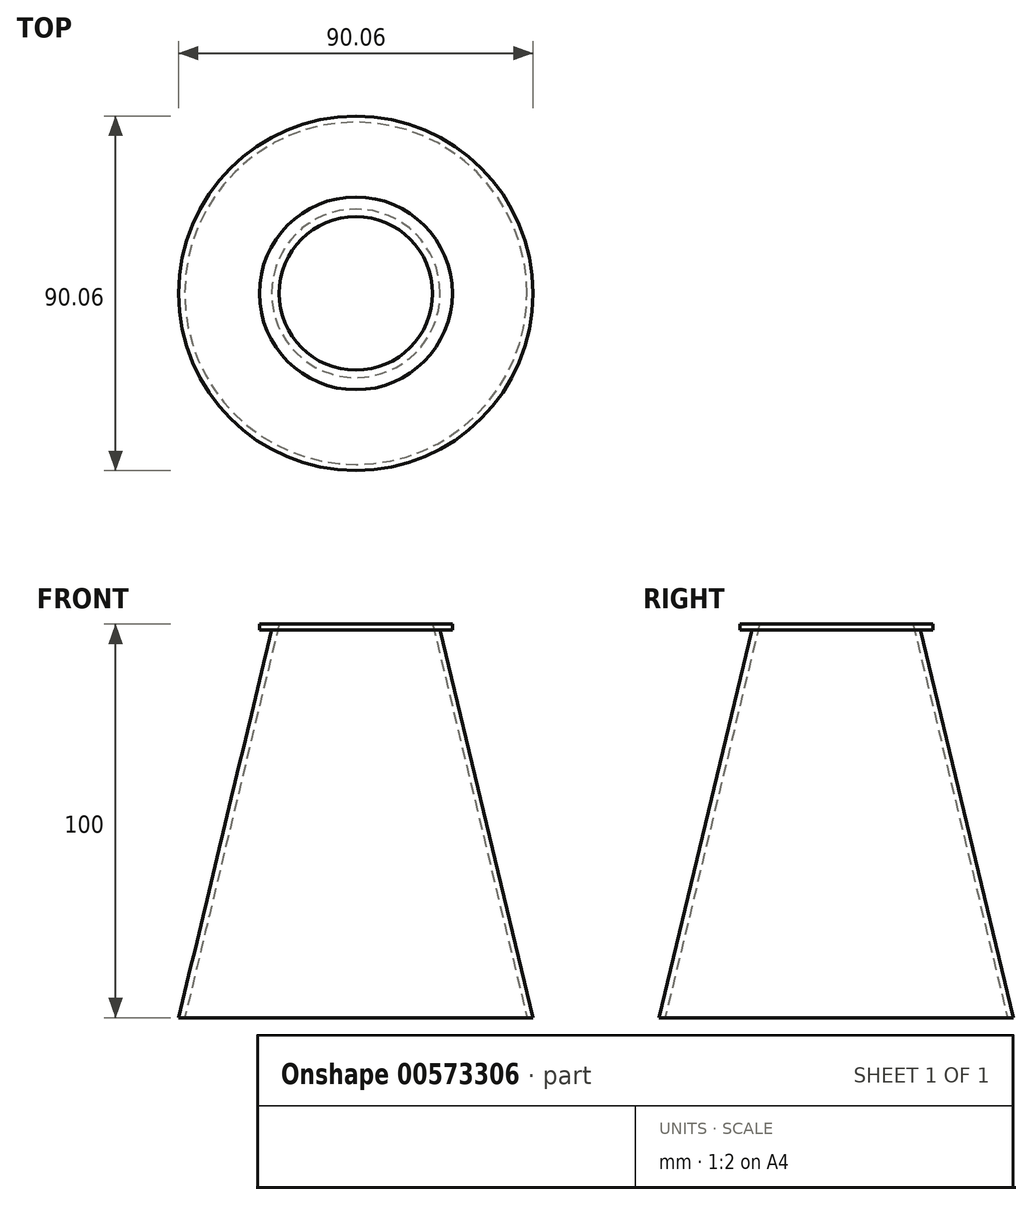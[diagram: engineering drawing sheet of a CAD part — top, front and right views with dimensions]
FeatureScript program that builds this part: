
annotation { "Feature Type Name" : "Feature", "Feature Type Description" : "" }
export const myFeature = defineFeature(function(context is Context, id is Id, definition is map)
    precondition{}
    {
        {
            var Q0;
            Q0=qCreatedBy(makeId("Front.planeOp"),FACE);
            var sketch = newSketch(context, id + "F0", { "sketchPlane" : qUnion([Q0])});
            skLineSegment(sketch, "E0.bottom", {"start": v(43.48, 0) * mm, "end": v(45.03, 0) * mm});
            skLineSegment(sketch, "E0.top", {"start": v(19.5, 100) * mm, "end": v(24.5, 100) * mm});
            skLineSegment(sketch, "E1", {"start": v(43.48, 0) * mm, "end": v(19.5, 100) * mm});
            skLineSegment(sketch, "E2", {"start": v(45.03, 0) * mm, "end": v(21.4, 98.5) * mm});
            skLineSegment(sketch, "E3", {"start": v(24.5, 98.5) * mm, "end": v(21.4, 98.5) * mm});
            skLineSegment(sketch, "E4", {"start": v(24.5, 98.5) * mm, "end": v(24.5, 100) * mm});
            skPoint(sketch, "E4.endSnap0", {"position": v(38.2, 100) * mm});
            skLineSegment(sketch, "E5", {"start": v(25.19, 82.73) * mm, "end": v(23.73, 82.38) * mm, "construction": true});
            skPoint(sketch, "E6", {"position": v(25, 83.5) * mm});
            skPoint(sketch, "E0.right.end.orphan", {"position": v(56.9, 100) * mm});
            skPoint(sketch, "E7.orphan", {"position": v(22.5, 0) * mm});
            skLineSegment(sketch, "E8", {"start": v(0, 0) * mm, "end": v(0, 65.1) * mm, "construction": true});
            skSolve(sketch);
        }
        {
            var Q0;
            Q0=makeQuery(id+"F0.imprint","IMPRINT",FACE,{"disambiguationData":[TD([[makeQuery(id+"F0.imprint","IMPRINT",EDGE,{"derivedFrom":sQuery(id+"F0.wireOp",EDGE,"E0.bottom")}),1.0]])]});
            var Q1;
            Q1=sQuery(id+"F0.wireOp",EDGE,"E8");
            revolve(context, id + "F1", {"entities" : qUnion([Q0]), "axis" : qUnion([Q1]), "revolveType" : RevolveType.FULL});
        }
    });
